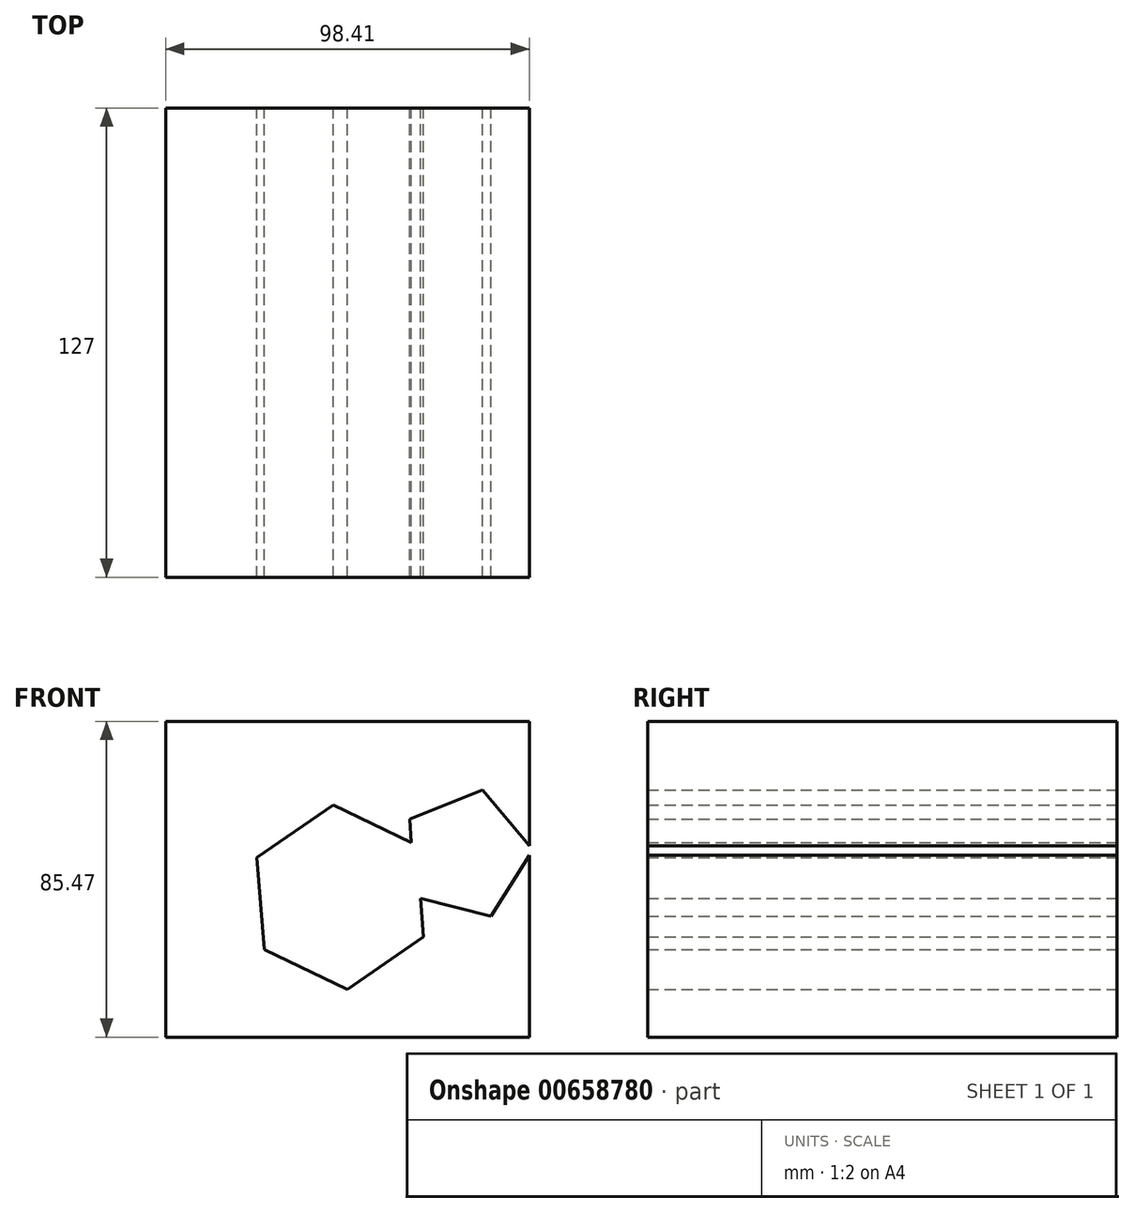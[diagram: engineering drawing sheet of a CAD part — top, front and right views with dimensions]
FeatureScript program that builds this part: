
annotation { "Feature Type Name" : "Feature", "Feature Type Description" : "" }
export const myFeature = defineFeature(function(context is Context, id is Id, definition is map)
    precondition{}
    {
        {
            var Q0;
            Q0=qCreatedBy(makeId("Front.planeOp"),FACE);
            var sketch = newSketch(context, id + "F0", { "sketchPlane" : qUnion([Q0])});
            skLineSegment(sketch, "E0.bottom", {"start": v(-47.25, -49.43) * mm, "end": v(51.16, -49.43) * mm});
            skLineSegment(sketch, "E0.top", {"start": v(-47.25, 36.04) * mm, "end": v(51.16, 36.04) * mm});
            skLineSegment(sketch, "E0.left", {"start": v(-47.25, -49.43) * mm, "end": v(-47.25, 36.04) * mm});
            skLineSegment(sketch, "E0.right", {"start": v(51.16, -49.43) * mm, "end": v(51.16, 36.04) * mm});
            skCircle(sketch, "E1.cCircle", {"center": v(0, -11.57) * mm, "radius": 25 * mm, "construction": true});
            skPoint(sketch, "E1.cCircle.perimeterSnap0", {"position": v(1.95, -49.43) * mm});
            skLineSegment(sketch, "E1.0", {"start": v(1.95, -36.48) * mm, "end": v(-20.6, -25.72) * mm});
            skPoint(sketch, "E1.0.startSnap0", {"position": v(1.95, -49.43) * mm});
            skLineSegment(sketch, "E1.1", {"start": v(-20.6, -25.72) * mm, "end": v(-22.56, -0.8) * mm});
            skLineSegment(sketch, "E1.2", {"start": v(-22.56, -0.8) * mm, "end": v(-1.95, 13.35) * mm});
            skLineSegment(sketch, "E1.3", {"start": v(-1.95, 13.35) * mm, "end": v(20.6, 2.58) * mm});
            skLineSegment(sketch, "E1.4", {"start": v(20.6, 2.58) * mm, "end": v(22.56, -22.33) * mm});
            skLineSegment(sketch, "E1.5", {"start": v(22.56, -22.33) * mm, "end": v(1.95, -36.48) * mm});
            skCircle(sketch, "E2.cCircle", {"center": v(34.06, 0) * mm, "radius": 18.03 * mm, "construction": true});
            skLineSegment(sketch, "E2.0", {"start": v(38.46, 17.48) * mm, "end": v(52.05, 1.22) * mm});
            skLineSegment(sketch, "E2.1", {"start": v(52.05, 1.22) * mm, "end": v(40.78, -16.73) * mm});
            skLineSegment(sketch, "E2.2", {"start": v(40.78, -16.73) * mm, "end": v(20.23, -11.56) * mm});
            skLineSegment(sketch, "E2.3", {"start": v(20.23, -11.56) * mm, "end": v(18.8, 9.58) * mm});
            skLineSegment(sketch, "E2.4", {"start": v(18.8, 9.58) * mm, "end": v(38.46, 17.48) * mm});
            skSolve(sketch);
        }
        {
            var Q0;
            {var subQ8=sQuery(id+"F0.wireOp",EDGE,"E0.bottom");Q0=makeQuery(id+"F0.imprint","IMPRINT",FACE,{"disambiguationData":[TD([[makeQuery(id+"F0.imprint","IMPRINT",EDGE,{"derivedFrom":subQ8}),1.0]])]});}
            extrude(context, id + "F1", {"entities" : qUnion([Q0]), "depth" : 127 * mm, "offsetDistance" : 25.4 * mm});
        }
    });
